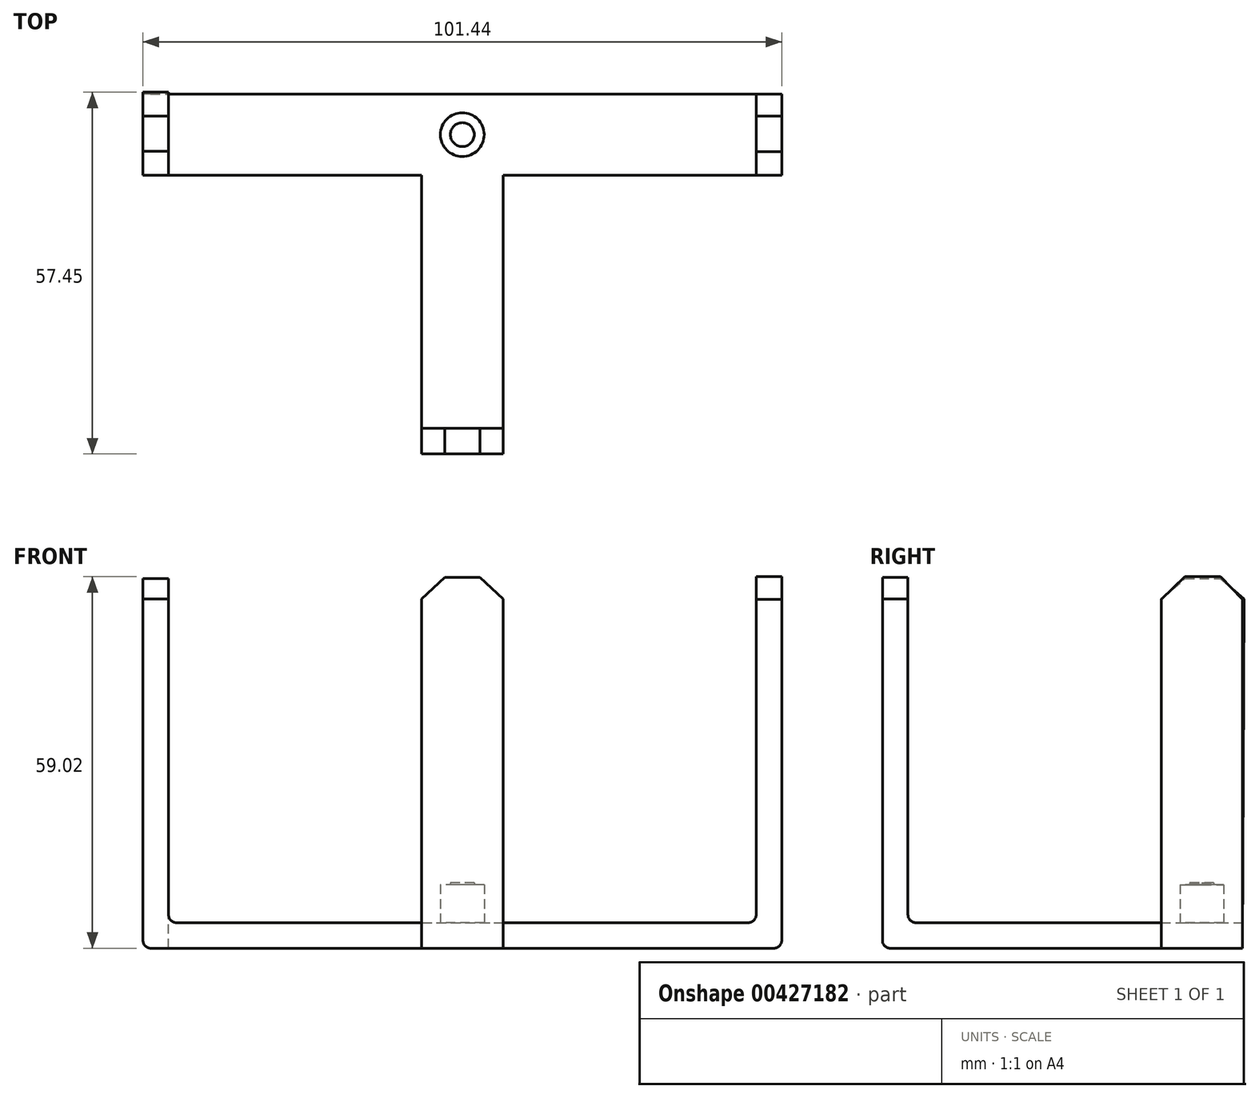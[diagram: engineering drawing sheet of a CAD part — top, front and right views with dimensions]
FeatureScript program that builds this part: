
annotation { "Feature Type Name" : "Feature", "Feature Type Description" : "" }
export const myFeature = defineFeature(function(context is Context, id is Id, definition is map)
    precondition{}
    {
        {
            var Q0;
            Q0=qCreatedBy(makeId("Top.planeOp"),FACE);
            var sketch = newSketch(context, id + "F0", { "sketchPlane" : qUnion([Q0])});
            skLineSegment(sketch, "E0.bottom", {"start": v(-50.72, 6.45) * mm, "end": v(50.72, 6.45) * mm});
            skLineSegment(sketch, "E0.top", {"start": v(-50.72, -6.45) * mm, "end": v(50.72, -6.45) * mm});
            skLineSegment(sketch, "E0.left", {"start": v(-50.72, 6.45) * mm, "end": v(-50.72, -6.45) * mm});
            skLineSegment(sketch, "E0.right", {"start": v(50.72, 6.45) * mm, "end": v(50.72, -6.45) * mm});
            skPoint(sketch, "E0.middle", {"position": v(0, 0) * mm});
            skSolve(sketch);
        }
        {
            var Q0;
            Q0=makeQuery(id+"F0.imprint","IMPRINT",FACE,{"disambiguationData":[TD([[makeQuery(id+"F0.imprint","IMPRINT",EDGE,{"derivedFrom":sQuery(id+"F0.wireOp",EDGE,"E0.bottom")}),-1.0]])]});
            extrude(context, id + "F1", {"entities" : qUnion([Q0]), "depth" : 4.06 * mm});
        }
        {
            var Q0;
            Q0=makeQuery(id+"F1.opExtrude","SWEPT_FACE",FACE,{"disambiguationData":[OSD([sQuery(id+"F0.wireOp",EDGE,"E0.right")])]});
            var sketch = newSketch(context, id + "F2", { "sketchPlane" : qUnion([Q0])});
            skLineSegment(sketch, "E1", {"start": v(-6.45, 0) * mm, "end": v(-6.45, 55.44) * mm});
            skLineSegment(sketch, "E2", {"start": v(-6.45, 55.44) * mm, "end": v(-2.68, 59.02) * mm});
            skLineSegment(sketch, "E3", {"start": v(6.45, 0) * mm, "end": v(6.45, 55.44) * mm});
            skLineSegment(sketch, "E4", {"start": v(-6.45, 55.44) * mm, "end": v(6.45, 55.44) * mm, "construction": true});
            skLineSegment(sketch, "E5", {"start": v(-2.68, 59.02) * mm, "end": v(2.94, 59.02) * mm});
            skLineSegment(sketch, "E6", {"start": v(2.94, 59.02) * mm, "end": v(6.45, 55.44) * mm});
            skLineSegment(sketch, "E7", {"start": v(-6.45, 0) * mm, "end": v(6.45, 0) * mm});
            skSolve(sketch);
        }
        {
            var Q0;
            {var subQ3=sQuery(id+"F2.wireOp",EDGE,"E2");Q0=makeQuery(id+"F2.imprint","IMPRINT",FACE,{"disambiguationData":[TD([[makeQuery(id+"F2.imprint","IMPRINT",EDGE,{"derivedFrom":subQ3}),-1.0]])]});}
            var Q1;
            {var subQ0=sQuery(id+"F2.wireOp",EDGE,"E7");Q1=makeQuery(id+"F2.imprint","IMPRINT",FACE,{"disambiguationData":[TD([[makeQuery(id+"F2.imprint","IMPRINT",EDGE,{"derivedFrom":subQ0}),-1.0]])]});}
            extrude(context, id + "F3", {"entities" : qUnion([Q0, Q1]), "operationType" : NewBodyOperationType.ADD, "oppositeDirection" : true, "depth" : 4.06 * mm});
        }
        {
            var Q0;
            Q0=makeQuery(id+"F1.opExtrude","SWEPT_FACE",FACE,{"disambiguationData":[OSD([sQuery(id+"F0.wireOp",EDGE,"E0.left")])]});
            var sketch = newSketch(context, id + "F4", { "sketchPlane" : qUnion([Q0])});
            skLineSegment(sketch, "E8", {"start": v(-6.45, 0) * mm, "end": v(6.45, 0) * mm});
            skLineSegment(sketch, "E9", {"start": v(6.45, 0) * mm, "end": v(6.45, 55.45) * mm});
            skLineSegment(sketch, "E10", {"start": v(6.45, 55.45) * mm, "end": v(2.66, 58.72) * mm});
            skLineSegment(sketch, "E11", {"start": v(2.66, 58.72) * mm, "end": v(-2.95, 58.72) * mm});
            skLineSegment(sketch, "E12", {"start": v(-2.95, 58.72) * mm, "end": v(-6.73, 55.45) * mm});
            skLineSegment(sketch, "E13", {"start": v(-6.73, 55.45) * mm, "end": v(-6.45, 0) * mm});
            skSolve(sketch);
        }
        {
            var Q0;
            {var subQ0=sQuery(id+"F4.wireOp",EDGE,"E10");Q0=makeQuery(id+"F4.imprint","IMPRINT",FACE,{"disambiguationData":[TD([[makeQuery(id+"F4.imprint","IMPRINT",EDGE,{"derivedFrom":subQ0}),1.0]])]});}
            var Q1;
            {var subQ0=sQuery(id+"F4.wireOp",EDGE,"E8");Q1=makeQuery(id+"F4.imprint","IMPRINT",FACE,{"disambiguationData":[TD([[makeQuery(id+"F4.imprint","IMPRINT",EDGE,{"derivedFrom":subQ0}),1.0]])]});}
            extrude(context, id + "F5", {"entities" : qUnion([Q0, Q1]), "operationType" : NewBodyOperationType.ADD, "oppositeDirection" : true, "depth" : 4.06 * mm});
        }
        {
            var Q0;
            Q0=qCreatedBy(makeId("Top.planeOp"),FACE);
            var sketch = newSketch(context, id + "F6", { "sketchPlane" : qUnion([Q0])});
            skLineSegment(sketch, "E14.bottom", {"start": v(6.45, -50.72) * mm, "end": v(-6.45, -50.72) * mm});
            skLineSegment(sketch, "E14.left", {"start": v(6.45, -50.72) * mm, "end": v(6.45, -6.25) * mm});
            skLineSegment(sketch, "E14.right", {"start": v(-6.45, -50.72) * mm, "end": v(-6.45, -6.25) * mm});
            skPoint(sketch, "E14.middle", {"position": v(0, 0) * mm});
            skLineSegment(sketch, "E15", {"start": v(6.45, -6.25) * mm, "end": v(-6.45, -6.25) * mm});
            skSolve(sketch);
        }
        {
            var Q0;
            Q0=makeQuery(id+"F6.imprint","IMPRINT",FACE,{"disambiguationData":[TD([[makeQuery(id+"F6.imprint","IMPRINT",EDGE,{"derivedFrom":sQuery(id+"F6.wireOp",EDGE,"E14.bottom")}),-1.0]])]});
            extrude(context, id + "F7", {"entities" : qUnion([Q0]), "operationType" : NewBodyOperationType.ADD, "depth" : 4.06 * mm});
        }
        {
            var Q0;
            Q0=makeQuery(id+"F7.opExtrude","SWEPT_FACE",FACE,{"disambiguationData":[OSD([sQuery(id+"F6.wireOp",EDGE,"E14.bottom")])]});
            var sketch = newSketch(context, id + "F8", { "sketchPlane" : qUnion([Q0])});
            skLineSegment(sketch, "E16", {"start": v(-6.45, 0) * mm, "end": v(6.45, 0) * mm});
            skLineSegment(sketch, "E17", {"start": v(6.45, 0) * mm, "end": v(6.45, 55.45) * mm});
            skLineSegment(sketch, "E18", {"start": v(6.45, 55.45) * mm, "end": v(2.8, 58.88) * mm});
            skLineSegment(sketch, "E19", {"start": v(2.8, 58.88) * mm, "end": v(-2.8, 58.88) * mm});
            skLineSegment(sketch, "E20", {"start": v(-2.8, 58.88) * mm, "end": v(-6.45, 55.45) * mm});
            skLineSegment(sketch, "E21", {"start": v(-6.45, 55.45) * mm, "end": v(-6.45, 0) * mm});
            skSolve(sketch);
        }
        {
            var Q0;
            {var subQ1=sQuery(id+"F8.wireOp",EDGE,"E18");Q0=makeQuery(id+"F8.imprint","IMPRINT",FACE,{"disambiguationData":[TD([[makeQuery(id+"F8.imprint","IMPRINT",EDGE,{"derivedFrom":subQ1}),1.0]])]});}
            var Q1;
            {var subQ0=sQuery(id+"F8.wireOp",EDGE,"E16");Q1=makeQuery(id+"F8.imprint","IMPRINT",FACE,{"disambiguationData":[TD([[makeQuery(id+"F8.imprint","IMPRINT",EDGE,{"derivedFrom":subQ0}),-1.0]])]});}
            extrude(context, id + "F9", {"entities" : qUnion([Q0, Q1]), "operationType" : NewBodyOperationType.ADD, "oppositeDirection" : true, "depth" : 4.06 * mm});
        }
        {
            var Q0;
            Q0=makeQuery(id+"F7.boolean.opBoolean","MERGE",FACE,{"derivedFrom":[makeQuery(id+"F1.opExtrude","CAP_FACE",FACE,{"disambiguationData":[OSD([sQuery(id+"F0.wireOp",EDGE,"E0.bottom"),sQuery(id+"F0.wireOp",EDGE,"E0.top"),sQuery(id+"F0.wireOp",EDGE,"E0.left"),sQuery(id+"F0.wireOp",EDGE,"E0.right")])],"isStart":false}),makeQuery(id+"F7.opExtrude","CAP_FACE",FACE,{"disambiguationData":[OSD([sQuery(id+"F6.wireOp",EDGE,"E14.bottom"),sQuery(id+"F6.wireOp",EDGE,"E14.left"),sQuery(id+"F6.wireOp",EDGE,"E14.right"),sQuery(id+"F6.wireOp",EDGE,"E15")])],"isStart":false})]});
            var sketch = newSketch(context, id + "F10", { "sketchPlane" : qUnion([Q0])});
            skCircle(sketch, "E22", {"center": v(0, 0) * mm, "radius": 3.48 * mm});
            skSolve(sketch);
        }
        {
            var Q0;
            Q0=makeQuery(id+"F10.imprint","IMPRINT",FACE,{"disambiguationData":[TD([[makeQuery(id+"F10.imprint","IMPRINT",EDGE,{"derivedFrom":sQuery(id+"F10.wireOp",EDGE,"E22")}),1.0]])]});
            extrude(context, id + "F11", {"entities" : qUnion([Q0]), "operationType" : NewBodyOperationType.ADD, "depth" : 6.02 * mm});
        }
        {
            var Q0;
            Q0=makeQuery(id+"F5.boolean.opBoolean","INTERSECT",EDGE,{"derivedFrom":[makeQuery(id+"F1.opExtrude","CAP_FACE",FACE,{"disambiguationData":[OSD([sQuery(id+"F0.wireOp",EDGE,"E0.bottom"),sQuery(id+"F0.wireOp",EDGE,"E0.top"),sQuery(id+"F0.wireOp",EDGE,"E0.left"),sQuery(id+"F0.wireOp",EDGE,"E0.right")])],"isStart":false}),makeQuery(id+"F5.opExtrude","CAP_FACE",FACE,{"disambiguationData":[OSD([sQuery(id+"F4.wireOp",EDGE,"E8"),sQuery(id+"F4.wireOp",EDGE,"E9"),sQuery(id+"F4.wireOp",EDGE,"E10"),sQuery(id+"F4.wireOp",EDGE,"E11"),sQuery(id+"F4.wireOp",EDGE,"E12"),sQuery(id+"F4.wireOp",EDGE,"E13")])],"isStart":false})]});
            var Q1;
            Q1=makeQuery(id+"F3.boolean.opBoolean","INTERSECT",EDGE,{"derivedFrom":[makeQuery(id+"F1.opExtrude","CAP_FACE",FACE,{"disambiguationData":[OSD([sQuery(id+"F0.wireOp",EDGE,"E0.bottom"),sQuery(id+"F0.wireOp",EDGE,"E0.top"),sQuery(id+"F0.wireOp",EDGE,"E0.left"),sQuery(id+"F0.wireOp",EDGE,"E0.right")])],"isStart":false}),makeQuery(id+"F3.opExtrude","CAP_FACE",FACE,{"disambiguationData":[OSD([sQuery(id+"F2.wireOp",EDGE,"E1"),sQuery(id+"F2.wireOp",EDGE,"E2"),sQuery(id+"F2.wireOp",EDGE,"E3"),sQuery(id+"F2.wireOp",EDGE,"E5"),sQuery(id+"F2.wireOp",EDGE,"E6"),sQuery(id+"F2.wireOp",EDGE,"E7")])],"isStart":false})]});
            var Q2;
            Q2=makeQuery(id+"F1.opExtrude","CAP_EDGE",EDGE,{"disambiguationData":[OSD([sQuery(id+"F0.wireOp",EDGE,"E0.right")])],"isStart":true});
            var Q3;
            Q3=makeQuery(id+"F1.opExtrude","CAP_EDGE",EDGE,{"disambiguationData":[OSD([sQuery(id+"F0.wireOp",EDGE,"E0.left")])],"isStart":true});
            var Q4;
            Q4=makeQuery(id+"F7.opExtrude","CAP_EDGE",EDGE,{"disambiguationData":[OSD([sQuery(id+"F6.wireOp",EDGE,"E14.bottom")])],"isStart":true});
            var Q5;
            Q5=makeQuery(id+"F9.boolean.opBoolean","INTERSECT",EDGE,{"derivedFrom":[makeQuery(id+"F7.boolean.opBoolean","MERGE",FACE,{"derivedFrom":[makeQuery(id+"F1.opExtrude","CAP_FACE",FACE,{"disambiguationData":[OSD([sQuery(id+"F0.wireOp",EDGE,"E0.bottom"),sQuery(id+"F0.wireOp",EDGE,"E0.top"),sQuery(id+"F0.wireOp",EDGE,"E0.left"),sQuery(id+"F0.wireOp",EDGE,"E0.right")])],"isStart":false}),makeQuery(id+"F7.opExtrude","CAP_FACE",FACE,{"disambiguationData":[OSD([sQuery(id+"F6.wireOp",EDGE,"E14.bottom"),sQuery(id+"F6.wireOp",EDGE,"E14.left"),sQuery(id+"F6.wireOp",EDGE,"E14.right"),sQuery(id+"F6.wireOp",EDGE,"E15")])],"isStart":false})]}),makeQuery(id+"F9.opExtrude","CAP_FACE",FACE,{"disambiguationData":[OSD([sQuery(id+"F8.wireOp",EDGE,"E16"),sQuery(id+"F8.wireOp",EDGE,"E17"),sQuery(id+"F8.wireOp",EDGE,"E18"),sQuery(id+"F8.wireOp",EDGE,"E19"),sQuery(id+"F8.wireOp",EDGE,"E20"),sQuery(id+"F8.wireOp",EDGE,"E21")])],"isStart":false})]});
            fillet(context, id + "F12", {"entities" : qUnion([Q0, Q1, Q2, Q3, Q4, Q5]), "radius" : 1.23 * mm, "tangentPropagation" : true, "allowEdgeOverflow" : false});
        }
        {
            var Q0;
            Q0=makeQuery(id+"F11.opExtrude","CAP_FACE",FACE,{"disambiguationData":[OSD([sQuery(id+"F10.wireOp",EDGE,"E22")])],"isStart":false});
            var sketch = newSketch(context, id + "F13", { "sketchPlane" : qUnion([Q0])});
            skCircle(sketch, "E23", {"center": v(0, 0) * mm, "radius": 1.9 * mm});
            skSolve(sketch);
        }
        {
            var Q0;
            Q0=makeQuery(id+"F13.imprint","IMPRINT",FACE,{"disambiguationData":[TD([[makeQuery(id+"F13.imprint","IMPRINT",EDGE,{"derivedFrom":sQuery(id+"F13.wireOp",EDGE,"E23")}),1.0]])]});
            extrude(context, id + "F14", {"entities" : qUnion([Q0]), "operationType" : NewBodyOperationType.ADD, "depth" : 0.28 * mm});
        }
    });
